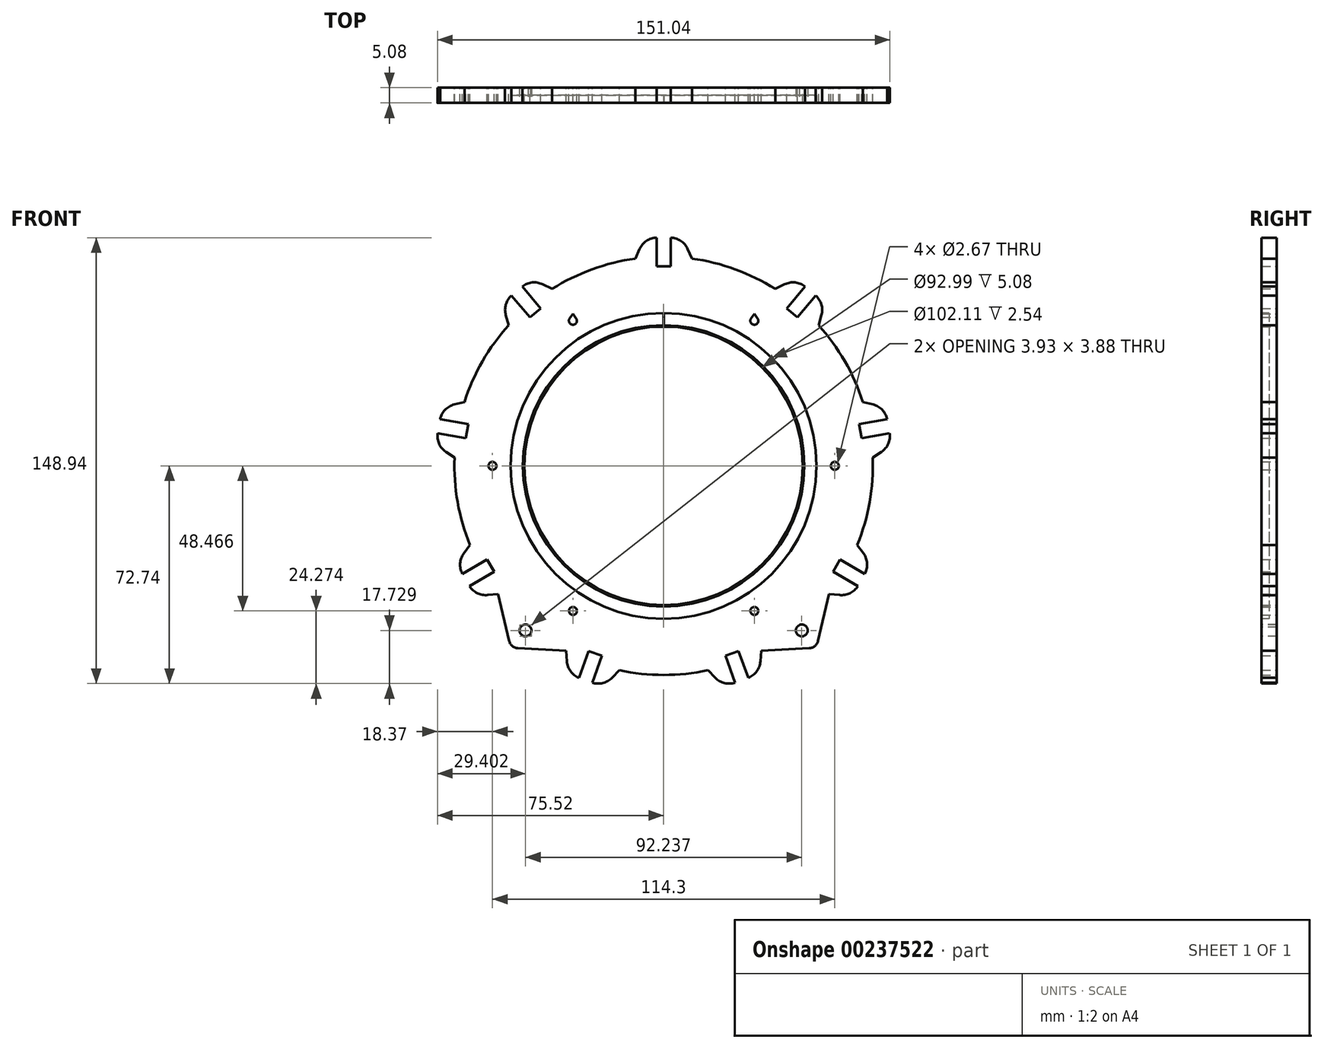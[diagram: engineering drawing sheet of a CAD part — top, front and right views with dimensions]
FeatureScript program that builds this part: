
annotation { "Feature Type Name" : "Feature", "Feature Type Description" : "" }
export const myFeature = defineFeature(function(context is Context, id is Id, definition is map)
    precondition{}
    {
        {
            var Q0;
            Q0=qCreatedBy(makeId("Front.planeOp"),FACE);
            var sketch = newSketch(context, id + "F0", { "sketchPlane" : qUnion([Q0])});
            skCircle(sketch, "E0", {"center": v(0, 0) * mm, "radius": 69.85 * mm});
            skCircle(sketch, "E1", {"center": v(0, 0) * mm, "radius": 46.5 * mm});
            skCircle(sketch, "E2", {"center": v(0, 0) * mm, "radius": 57.15 * mm, "construction": true});
            skPoint(sketch, "E3.center", {"position": v(0, -7.06) * mm});
            skLineSegment(sketch, "E4", {"start": v(-9.44, 69.2) * mm, "end": v(-8.02, 72.42) * mm});
            skLineSegment(sketch, "E5", {"start": v(-2.21, 76.2) * mm, "end": v(2.21, 76.2) * mm});
            skLineSegment(sketch, "E6", {"start": v(8.02, 72.42) * mm, "end": v(9.44, 69.2) * mm});
            skPoint(sketch, "E7", {"position": v(0, 76.2) * mm});
            skLineSegment(sketch, "E8", {"start": v(-2.35, 76.2) * mm, "end": v(-2.35, 66.67) * mm});
            skLineSegment(sketch, "E9", {"start": v(-2.35, 66.67) * mm, "end": v(2.35, 66.67) * mm});
            skLineSegment(sketch, "E10", {"start": v(2.35, 66.67) * mm, "end": v(2.35, 76.2) * mm});
            skPoint(sketch, "E11", {"position": v(0, 66.67) * mm});
            skPoint(sketch, "E12.visualSharp", {"position": v(-6.35, 76.2) * mm});
            skArc(sketch, "E12.filletArc", {"start": v(-2.21, 76.2) * mm, "mid": v(-5.68, 75.17) * mm, "end": v(-8.02, 72.42) * mm});
            skPoint(sketch, "E13.visualSharp", {"position": v(6.35, 76.2) * mm});
            skArc(sketch, "E13.filletArc", {"start": v(8.02, 72.42) * mm, "mid": v(5.68, 75.17) * mm, "end": v(2.21, 76.2) * mm});
            skCircle(sketch, "E14", {"center": v(0, 0) * mm, "radius": 66.72 * mm, "construction": true});
            skLineSegment(sketch, "E15.1.0", {"start": v(-51.72, 46.95) * mm, "end": v(-52.7, 50.32) * mm});
            skArc(sketch, "E15.1.1", {"start": v(-50.68, 56.95) * mm, "mid": v(-52.67, 53.93) * mm, "end": v(-52.7, 50.32) * mm});
            skLineSegment(sketch, "E15.1.2", {"start": v(-50.78, 56.86) * mm, "end": v(-44.66, 49.57) * mm});
            skLineSegment(sketch, "E15.1.3", {"start": v(-41.06, 52.59) * mm, "end": v(-47.18, 59.88) * mm});
            skArc(sketch, "E15.1.4", {"start": v(-40.4, 60.63) * mm, "mid": v(-43.97, 61.23) * mm, "end": v(-47.29, 59.8) * mm});
            skLineSegment(sketch, "E15.1.5", {"start": v(-40.4, 60.63) * mm, "end": v(-37.26, 59.08) * mm});
            skLineSegment(sketch, "E15.1.6", {"start": v(-44.66, 49.57) * mm, "end": v(-41.06, 52.59) * mm});
            skLineSegment(sketch, "E15.2.0", {"start": v(-69.8, 2.72) * mm, "end": v(-72.7, 4.68) * mm});
            skArc(sketch, "E15.2.1", {"start": v(-75.43, 11.05) * mm, "mid": v(-75.01, 7.46) * mm, "end": v(-72.7, 4.68) * mm});
            skLineSegment(sketch, "E15.2.2", {"start": v(-75.45, 10.92) * mm, "end": v(-66.07, 9.26) * mm});
            skLineSegment(sketch, "E15.2.3", {"start": v(-65.25, 13.9) * mm, "end": v(-74.63, 15.55) * mm});
            skArc(sketch, "E15.2.4", {"start": v(-69.92, 20.47) * mm, "mid": v(-73.04, 18.65) * mm, "end": v(-74.66, 15.41) * mm});
            skLineSegment(sketch, "E15.2.5", {"start": v(-69.92, 20.47) * mm, "end": v(-66.52, 21.31) * mm});
            skLineSegment(sketch, "E15.2.6", {"start": v(-66.07, 9.26) * mm, "end": v(-65.25, 13.9) * mm});
            skLineSegment(sketch, "E15.3.0", {"start": v(-55.22, -42.78) * mm, "end": v(-58.7, -43.15) * mm});
            skArc(sketch, "E15.3.1", {"start": v(-64.88, -40.02) * mm, "mid": v(-62.26, -42.5) * mm, "end": v(-58.7, -43.15) * mm});
            skLineSegment(sketch, "E15.3.2", {"start": v(-64.82, -40.13) * mm, "end": v(-56.57, -35.37) * mm});
            skLineSegment(sketch, "E15.3.3", {"start": v(-58.92, -31.3) * mm, "end": v(-67.17, -36.07) * mm});
            skArc(sketch, "E15.3.4", {"start": v(-66.72, -29.26) * mm, "mid": v(-67.94, -32.67) * mm, "end": v(-67.1, -36.18) * mm});
            skLineSegment(sketch, "E15.3.5", {"start": v(-66.72, -29.26) * mm, "end": v(-64.66, -26.43) * mm});
            skLineSegment(sketch, "E15.3.6", {"start": v(-56.57, -35.37) * mm, "end": v(-58.92, -31.3) * mm});
            skLineSegment(sketch, "E15.4.0", {"start": v(-14.8, -68.26) * mm, "end": v(-17.23, -70.8) * mm});
            skArc(sketch, "E15.4.1", {"start": v(-23.98, -72.36) * mm, "mid": v(-20.37, -72.58) * mm, "end": v(-17.23, -70.8) * mm});
            skLineSegment(sketch, "E15.4.2", {"start": v(-23.85, -72.4) * mm, "end": v(-20.6, -63.46) * mm});
            skLineSegment(sketch, "E15.4.3", {"start": v(-25.01, -61.85) * mm, "end": v(-28.27, -70.8) * mm});
            skArc(sketch, "E15.4.4", {"start": v(-32.3, -65.3) * mm, "mid": v(-31.05, -68.7) * mm, "end": v(-28.14, -70.85) * mm});
            skLineSegment(sketch, "E15.4.5", {"start": v(-32.3, -65.3) * mm, "end": v(-32.54, -61.8) * mm});
            skLineSegment(sketch, "E15.4.6", {"start": v(-20.6, -63.46) * mm, "end": v(-25.01, -61.85) * mm});
            skLineSegment(sketch, "E15.5.0", {"start": v(32.54, -61.8) * mm, "end": v(32.3, -65.3) * mm});
            skArc(sketch, "E15.5.1", {"start": v(28.14, -70.85) * mm, "mid": v(31.05, -68.7) * mm, "end": v(32.3, -65.3) * mm});
            skLineSegment(sketch, "E15.5.2", {"start": v(28.27, -70.8) * mm, "end": v(25.01, -61.85) * mm});
            skLineSegment(sketch, "E15.5.3", {"start": v(20.6, -63.46) * mm, "end": v(23.85, -72.4) * mm});
            skArc(sketch, "E15.5.4", {"start": v(17.23, -70.8) * mm, "mid": v(20.37, -72.58) * mm, "end": v(23.98, -72.36) * mm});
            skLineSegment(sketch, "E15.5.5", {"start": v(17.23, -70.8) * mm, "end": v(14.8, -68.26) * mm});
            skLineSegment(sketch, "E15.5.6", {"start": v(25.01, -61.85) * mm, "end": v(20.6, -63.46) * mm});
            skLineSegment(sketch, "E15.6.0", {"start": v(64.66, -26.43) * mm, "end": v(66.72, -29.26) * mm});
            skArc(sketch, "E15.6.1", {"start": v(67.1, -36.18) * mm, "mid": v(67.94, -32.67) * mm, "end": v(66.72, -29.26) * mm});
            skLineSegment(sketch, "E15.6.2", {"start": v(67.17, -36.07) * mm, "end": v(58.92, -31.3) * mm});
            skLineSegment(sketch, "E15.6.3", {"start": v(56.57, -35.37) * mm, "end": v(64.82, -40.13) * mm});
            skArc(sketch, "E15.6.4", {"start": v(58.7, -43.15) * mm, "mid": v(62.26, -42.5) * mm, "end": v(64.88, -40.02) * mm});
            skLineSegment(sketch, "E15.6.5", {"start": v(58.7, -43.15) * mm, "end": v(55.22, -42.78) * mm});
            skLineSegment(sketch, "E15.6.6", {"start": v(58.92, -31.3) * mm, "end": v(56.57, -35.37) * mm});
            skLineSegment(sketch, "E15.7.0", {"start": v(66.52, 21.31) * mm, "end": v(69.92, 20.47) * mm});
            skArc(sketch, "E15.7.1", {"start": v(74.66, 15.41) * mm, "mid": v(73.04, 18.65) * mm, "end": v(69.92, 20.47) * mm});
            skLineSegment(sketch, "E15.7.2", {"start": v(74.63, 15.55) * mm, "end": v(65.25, 13.9) * mm});
            skLineSegment(sketch, "E15.7.3", {"start": v(66.07, 9.26) * mm, "end": v(75.45, 10.92) * mm});
            skArc(sketch, "E15.7.4", {"start": v(72.7, 4.68) * mm, "mid": v(75.01, 7.46) * mm, "end": v(75.43, 11.05) * mm});
            skLineSegment(sketch, "E15.7.5", {"start": v(72.7, 4.68) * mm, "end": v(69.8, 2.72) * mm});
            skLineSegment(sketch, "E15.7.6", {"start": v(65.25, 13.9) * mm, "end": v(66.07, 9.26) * mm});
            skLineSegment(sketch, "E15.8.0", {"start": v(37.26, 59.08) * mm, "end": v(40.4, 60.63) * mm});
            skArc(sketch, "E15.8.1", {"start": v(47.29, 59.8) * mm, "mid": v(43.97, 61.23) * mm, "end": v(40.4, 60.63) * mm});
            skLineSegment(sketch, "E15.8.2", {"start": v(47.18, 59.88) * mm, "end": v(41.06, 52.59) * mm});
            skLineSegment(sketch, "E15.8.3", {"start": v(44.66, 49.57) * mm, "end": v(50.78, 56.86) * mm});
            skArc(sketch, "E15.8.4", {"start": v(52.7, 50.32) * mm, "mid": v(52.67, 53.93) * mm, "end": v(50.68, 56.95) * mm});
            skLineSegment(sketch, "E15.8.5", {"start": v(52.7, 50.32) * mm, "end": v(51.72, 46.95) * mm});
            skLineSegment(sketch, "E15.8.6", {"start": v(41.06, 52.59) * mm, "end": v(44.66, 49.57) * mm});
            skCircle(sketch, "E16", {"center": v(57.15, 0) * mm, "radius": 1.33 * mm});
            skCircle(sketch, "E17", {"center": v(30.28, 48.47) * mm, "radius": 1.33 * mm});
            skCircle(sketch, "E18", {"center": v(30.28, -48.47) * mm, "radius": 1.33 * mm});
            skLineSegment(sketch, "E19", {"start": v(0, 0) * mm, "end": v(30.28, -48.47) * mm, "construction": true});
            skLineSegment(sketch, "E20", {"start": v(30.28, 48.47) * mm, "end": v(0, 0) * mm, "construction": true});
            skCircle(sketch, "E21.MirrorC", {"center": v(-30.28, -48.47) * mm, "radius": 1.33 * mm});
            skCircle(sketch, "E22.MirrorC", {"center": v(-57.15, 0) * mm, "radius": 1.33 * mm});
            skCircle(sketch, "E23.MirrorC", {"center": v(-30.28, 48.47) * mm, "radius": 1.33 * mm});
            skLineSegment(sketch, "E24", {"start": v(31.38, 49.23) * mm, "end": v(30.28, 50.78) * mm});
            skLineSegment(sketch, "E25", {"start": v(30.28, 50.78) * mm, "end": v(29.2, 49.23) * mm});
            skLineSegment(sketch, "E26", {"start": v(-31.38, 49.23) * mm, "end": v(-30.28, 50.78) * mm});
            skLineSegment(sketch, "E27", {"start": v(-30.28, 50.78) * mm, "end": v(-29.2, 49.23) * mm});
            skArc(sketch, "E28", {"start": v(-2.21, 76.2) * mm, "mid": v(-8.62, 74.13) * mm, "end": v(-12.61, 68.7) * mm});
            skArc(sketch, "E29", {"start": v(12.61, 68.7) * mm, "mid": v(8.7, 74.13) * mm, "end": v(2.35, 76.2) * mm});
            skSolve(sketch);
        }
        {
            var Q0;
            Q0=makeQuery(id+"F0.imprint","IMPRINT",FACE,{"disambiguationData":[TD([[makeQuery(id+"F0.imprint","IMPRINT",EDGE,{"derivedFrom":sQuery(id+"F0.wireOp",EDGE,"E1")}),-1.0]])]});
            var Q1;
            {var subQ0=sQuery(id+"F0.wireOp",EDGE,"E15.1.5");Q1=makeQuery(id+"F0.imprint","IMPRINT",FACE,{"disambiguationData":[TD([[makeQuery(id+"F0.imprint","IMPRINT",EDGE,{"derivedFrom":subQ0}),-1.0]])]});}
            var Q2;
            {var subQ0=sQuery(id+"F0.wireOp",EDGE,"E15.1.0");Q2=makeQuery(id+"F0.imprint","IMPRINT",FACE,{"disambiguationData":[TD([[makeQuery(id+"F0.imprint","IMPRINT",EDGE,{"derivedFrom":subQ0}),-1.0]])]});}
            var Q3;
            {var subQ0=sQuery(id+"F0.wireOp",EDGE,"E4");Q3=makeQuery(id+"F0.imprint","IMPRINT",FACE,{"disambiguationData":[TD([[makeQuery(id+"F0.imprint","IMPRINT",EDGE,{"derivedFrom":subQ0}),-1.0]])]});}
            var Q4;
            {var subQ0=sQuery(id+"F0.wireOp",EDGE,"E6");Q4=makeQuery(id+"F0.imprint","IMPRINT",FACE,{"disambiguationData":[TD([[makeQuery(id+"F0.imprint","IMPRINT",EDGE,{"derivedFrom":subQ0}),-1.0]])]});}
            var Q5;
            {var subQ0=sQuery(id+"F0.wireOp",EDGE,"E15.8.0");Q5=makeQuery(id+"F0.imprint","IMPRINT",FACE,{"disambiguationData":[TD([[makeQuery(id+"F0.imprint","IMPRINT",EDGE,{"derivedFrom":subQ0}),-1.0]])]});}
            var Q6;
            {var subQ0=sQuery(id+"F0.wireOp",EDGE,"E15.8.5");Q6=makeQuery(id+"F0.imprint","IMPRINT",FACE,{"disambiguationData":[TD([[makeQuery(id+"F0.imprint","IMPRINT",EDGE,{"derivedFrom":subQ0}),-1.0]])]});}
            var Q7;
            {var subQ0=sQuery(id+"F0.wireOp",EDGE,"E15.7.0");Q7=makeQuery(id+"F0.imprint","IMPRINT",FACE,{"disambiguationData":[TD([[makeQuery(id+"F0.imprint","IMPRINT",EDGE,{"derivedFrom":subQ0}),-1.0]])]});}
            var Q8;
            {var subQ0=sQuery(id+"F0.wireOp",EDGE,"E15.7.5");Q8=makeQuery(id+"F0.imprint","IMPRINT",FACE,{"disambiguationData":[TD([[makeQuery(id+"F0.imprint","IMPRINT",EDGE,{"derivedFrom":subQ0}),-1.0]])]});}
            var Q9;
            {var subQ0=sQuery(id+"F0.wireOp",EDGE,"E15.6.0");Q9=makeQuery(id+"F0.imprint","IMPRINT",FACE,{"disambiguationData":[TD([[makeQuery(id+"F0.imprint","IMPRINT",EDGE,{"derivedFrom":subQ0}),-1.0]])]});}
            var Q10;
            {var subQ0=sQuery(id+"F0.wireOp",EDGE,"E15.6.5");Q10=makeQuery(id+"F0.imprint","IMPRINT",FACE,{"disambiguationData":[TD([[makeQuery(id+"F0.imprint","IMPRINT",EDGE,{"derivedFrom":subQ0}),-1.0]])]});}
            var Q11;
            {var subQ0=sQuery(id+"F0.wireOp",EDGE,"E15.5.5");Q11=makeQuery(id+"F0.imprint","IMPRINT",FACE,{"disambiguationData":[TD([[makeQuery(id+"F0.imprint","IMPRINT",EDGE,{"derivedFrom":subQ0}),-1.0]])]});}
            var Q12;
            {var subQ0=sQuery(id+"F0.wireOp",EDGE,"E15.5.0");Q12=makeQuery(id+"F0.imprint","IMPRINT",FACE,{"disambiguationData":[TD([[makeQuery(id+"F0.imprint","IMPRINT",EDGE,{"derivedFrom":subQ0}),-1.0]])]});}
            var Q13;
            {var subQ0=sQuery(id+"F0.wireOp",EDGE,"E15.4.5");Q13=makeQuery(id+"F0.imprint","IMPRINT",FACE,{"disambiguationData":[TD([[makeQuery(id+"F0.imprint","IMPRINT",EDGE,{"derivedFrom":subQ0}),-1.0]])]});}
            var Q14;
            {var subQ0=sQuery(id+"F0.wireOp",EDGE,"E15.4.0");Q14=makeQuery(id+"F0.imprint","IMPRINT",FACE,{"disambiguationData":[TD([[makeQuery(id+"F0.imprint","IMPRINT",EDGE,{"derivedFrom":subQ0}),-1.0]])]});}
            var Q15;
            {var subQ0=sQuery(id+"F0.wireOp",EDGE,"E15.3.0");Q15=makeQuery(id+"F0.imprint","IMPRINT",FACE,{"disambiguationData":[TD([[makeQuery(id+"F0.imprint","IMPRINT",EDGE,{"derivedFrom":subQ0}),-1.0]])]});}
            var Q16;
            {var subQ0=sQuery(id+"F0.wireOp",EDGE,"E15.3.5");Q16=makeQuery(id+"F0.imprint","IMPRINT",FACE,{"disambiguationData":[TD([[makeQuery(id+"F0.imprint","IMPRINT",EDGE,{"derivedFrom":subQ0}),-1.0]])]});}
            var Q17;
            {var subQ0=sQuery(id+"F0.wireOp",EDGE,"E15.2.0");Q17=makeQuery(id+"F0.imprint","IMPRINT",FACE,{"disambiguationData":[TD([[makeQuery(id+"F0.imprint","IMPRINT",EDGE,{"derivedFrom":subQ0}),-1.0]])]});}
            var Q18;
            {var subQ0=sQuery(id+"F0.wireOp",EDGE,"E15.2.5");Q18=makeQuery(id+"F0.imprint","IMPRINT",FACE,{"disambiguationData":[TD([[makeQuery(id+"F0.imprint","IMPRINT",EDGE,{"derivedFrom":subQ0}),-1.0]])]});}
            extrude(context, id + "F1", {"entities" : qUnion([Q0, Q1, Q2, Q3, Q4, Q5, Q6, Q7, Q8, Q9, Q10, Q11, Q12, Q13, Q14, Q15, Q16, Q17, Q18]), "depth" : 5.08 * mm});
        }
        {
            var Q0;
            Q0=makeQuery(id+"F1.opExtrude","CAP_FACE",FACE,{"disambiguationData":[OSD([sQuery(id+"F0.wireOp",EDGE,"E0"),sQuery(id+"F0.wireOp",EDGE,"E1"),sQuery(id+"F0.wireOp",EDGE,"s7rXqqL2-3z2l-88EV-UIsY-hwb08Po9ZJjJ"),sQuery(id+"F0.wireOp",EDGE,"E3.1.0"),sQuery(id+"F0.wireOp",EDGE,"E3.2.0"),sQuery(id+"F0.wireOp",EDGE,"E3.3.0"),sQuery(id+"F0.wireOp",EDGE,"E4"),sQuery(id+"F0.wireOp",EDGE,"E6"),sQuery(id+"F0.wireOp",EDGE,"E8"),sQuery(id+"F0.wireOp",EDGE,"E9"),sQuery(id+"F0.wireOp",EDGE,"E10"),sQuery(id+"F0.wireOp",EDGE,"E12.filletArc"),sQuery(id+"F0.wireOp",EDGE,"E13.filletArc"),sQuery(id+"F0.wireOp",EDGE,"e3144966-756d-47fd-8283-5f46bd2110e0.1.0"),sQuery(id+"F0.wireOp",EDGE,"e3144966-756d-47fd-8283-5f46bd2110e0.1.1"),sQuery(id+"F0.wireOp",EDGE,"e3144966-756d-47fd-8283-5f46bd2110e0.1.2"),sQuery(id+"F0.wireOp",EDGE,"e3144966-756d-47fd-8283-5f46bd2110e0.1.3"),sQuery(id+"F0.wireOp",EDGE,"e3144966-756d-47fd-8283-5f46bd2110e0.1.4"),sQuery(id+"F0.wireOp",EDGE,"e3144966-756d-47fd-8283-5f46bd2110e0.1.6"),sQuery(id+"F0.wireOp",EDGE,"e3144966-756d-47fd-8283-5f46bd2110e0.1.7"),sQuery(id+"F0.wireOp",EDGE,"e3144966-756d-47fd-8283-5f46bd2110e0.2.0"),sQuery(id+"F0.wireOp",EDGE,"e3144966-756d-47fd-8283-5f46bd2110e0.2.1"),sQuery(id+"F0.wireOp",EDGE,"e3144966-756d-47fd-8283-5f46bd2110e0.2.2"),sQuery(id+"F0.wireOp",EDGE,"e3144966-756d-47fd-8283-5f46bd2110e0.2.3"),sQuery(id+"F0.wireOp",EDGE,"e3144966-756d-47fd-8283-5f46bd2110e0.2.4"),sQuery(id+"F0.wireOp",EDGE,"e3144966-756d-47fd-8283-5f46bd2110e0.2.6"),sQuery(id+"F0.wireOp",EDGE,"e3144966-756d-47fd-8283-5f46bd2110e0.2.7"),sQuery(id+"F0.wireOp",EDGE,"e3144966-756d-47fd-8283-5f46bd2110e0.3.0"),sQuery(id+"F0.wireOp",EDGE,"e3144966-756d-47fd-8283-5f46bd2110e0.3.1"),sQuery(id+"F0.wireOp",EDGE,"e3144966-756d-47fd-8283-5f46bd2110e0.3.2"),sQuery(id+"F0.wireOp",EDGE,"e3144966-756d-47fd-8283-5f46bd2110e0.3.3"),sQuery(id+"F0.wireOp",EDGE,"e3144966-756d-47fd-8283-5f46bd2110e0.3.4"),sQuery(id+"F0.wireOp",EDGE,"e3144966-756d-47fd-8283-5f46bd2110e0.3.6"),sQuery(id+"F0.wireOp",EDGE,"e3144966-756d-47fd-8283-5f46bd2110e0.3.7"),sQuery(id+"F0.wireOp",EDGE,"e3144966-756d-47fd-8283-5f46bd2110e0.4.0"),sQuery(id+"F0.wireOp",EDGE,"e3144966-756d-47fd-8283-5f46bd2110e0.4.1"),sQuery(id+"F0.wireOp",EDGE,"e3144966-756d-47fd-8283-5f46bd2110e0.4.2"),sQuery(id+"F0.wireOp",EDGE,"e3144966-756d-47fd-8283-5f46bd2110e0.4.3"),sQuery(id+"F0.wireOp",EDGE,"e3144966-756d-47fd-8283-5f46bd2110e0.4.4"),sQuery(id+"F0.wireOp",EDGE,"e3144966-756d-47fd-8283-5f46bd2110e0.4.6"),sQuery(id+"F0.wireOp",EDGE,"e3144966-756d-47fd-8283-5f46bd2110e0.4.7"),sQuery(id+"F0.wireOp",EDGE,"e3144966-756d-47fd-8283-5f46bd2110e0.5.0"),sQuery(id+"F0.wireOp",EDGE,"e3144966-756d-47fd-8283-5f46bd2110e0.5.1"),sQuery(id+"F0.wireOp",EDGE,"e3144966-756d-47fd-8283-5f46bd2110e0.5.2"),sQuery(id+"F0.wireOp",EDGE,"e3144966-756d-47fd-8283-5f46bd2110e0.5.3"),sQuery(id+"F0.wireOp",EDGE,"e3144966-756d-47fd-8283-5f46bd2110e0.5.4"),sQuery(id+"F0.wireOp",EDGE,"e3144966-756d-47fd-8283-5f46bd2110e0.5.6"),sQuery(id+"F0.wireOp",EDGE,"e3144966-756d-47fd-8283-5f46bd2110e0.5.7"),sQuery(id+"F0.wireOp",EDGE,"e3144966-756d-47fd-8283-5f46bd2110e0.6.0"),sQuery(id+"F0.wireOp",EDGE,"e3144966-756d-47fd-8283-5f46bd2110e0.6.1"),sQuery(id+"F0.wireOp",EDGE,"e3144966-756d-47fd-8283-5f46bd2110e0.6.2"),sQuery(id+"F0.wireOp",EDGE,"e3144966-756d-47fd-8283-5f46bd2110e0.6.3"),sQuery(id+"F0.wireOp",EDGE,"e3144966-756d-47fd-8283-5f46bd2110e0.6.4"),sQuery(id+"F0.wireOp",EDGE,"e3144966-756d-47fd-8283-5f46bd2110e0.6.6"),sQuery(id+"F0.wireOp",EDGE,"e3144966-756d-47fd-8283-5f46bd2110e0.6.7"),sQuery(id+"F0.wireOp",EDGE,"e3144966-756d-47fd-8283-5f46bd2110e0.7.0"),sQuery(id+"F0.wireOp",EDGE,"e3144966-756d-47fd-8283-5f46bd2110e0.7.1"),sQuery(id+"F0.wireOp",EDGE,"e3144966-756d-47fd-8283-5f46bd2110e0.7.2"),sQuery(id+"F0.wireOp",EDGE,"e3144966-756d-47fd-8283-5f46bd2110e0.7.3"),sQuery(id+"F0.wireOp",EDGE,"e3144966-756d-47fd-8283-5f46bd2110e0.7.4"),sQuery(id+"F0.wireOp",EDGE,"e3144966-756d-47fd-8283-5f46bd2110e0.7.6"),sQuery(id+"F0.wireOp",EDGE,"e3144966-756d-47fd-8283-5f46bd2110e0.7.7"),sQuery(id+"F0.wireOp",EDGE,"e3144966-756d-47fd-8283-5f46bd2110e0.8.0"),sQuery(id+"F0.wireOp",EDGE,"e3144966-756d-47fd-8283-5f46bd2110e0.8.1"),sQuery(id+"F0.wireOp",EDGE,"e3144966-756d-47fd-8283-5f46bd2110e0.8.2"),sQuery(id+"F0.wireOp",EDGE,"e3144966-756d-47fd-8283-5f46bd2110e0.8.3"),sQuery(id+"F0.wireOp",EDGE,"e3144966-756d-47fd-8283-5f46bd2110e0.8.4"),sQuery(id+"F0.wireOp",EDGE,"e3144966-756d-47fd-8283-5f46bd2110e0.8.6"),sQuery(id+"F0.wireOp",EDGE,"e3144966-756d-47fd-8283-5f46bd2110e0.8.7")])],"isStart":false});
            var sketch = newSketch(context, id + "F2", { "sketchPlane" : qUnion([Q0])});
            skCircle(sketch, "E30", {"center": v(0, 0) * mm, "radius": 47 * mm});
            skCircle(sketch, "E31", {"center": v(0, 0) * mm, "radius": 51.05 * mm});
            skSolve(sketch);
        }
        {
            var Q0;
            Q0=makeQuery(id+"F2.imprint","IMPRINT",FACE,{"disambiguationData":[TD([[makeQuery(id+"F2.imprint","IMPRINT",EDGE,{"derivedFrom":sQuery(id+"F2.wireOp",EDGE,"E31")}),1.0]])]});
            extrude(context, id + "F3", {"entities" : qUnion([Q0]), "operationType" : NewBodyOperationType.REMOVE, "oppositeDirection" : true, "depth" : 2.54 * mm});
        }
        {
            var Q0;
            {var subQ0=sQuery(id+"F0.wireOp",EDGE,"E15.5.2");var subQ1=sQuery(id+"F0.wireOp",EDGE,"E15.5.0");var subQ2=sQuery(id+"F0.wireOp",EDGE,"E15.5.5");var subQ3=sQuery(id+"F0.wireOp",EDGE,"E15.4.5");var subQ4=sQuery(id+"F0.wireOp",EDGE,"E15.4.6");var subQ5=sQuery(id+"F0.wireOp",EDGE,"E15.4.4");var subQ6=sQuery(id+"F0.wireOp",EDGE,"E15.5.3");var subQ7=sQuery(id+"F0.wireOp",EDGE,"E15.4.2");var subQ8=sQuery(id+"F0.wireOp",EDGE,"E15.4.0");var subQ9=sQuery(id+"F0.wireOp",EDGE,"E15.3.5");var subQ10=sQuery(id+"F0.wireOp",EDGE,"E15.3.3");var subQ11=sQuery(id+"F0.wireOp",EDGE,"E15.2.5");var subQ12=sQuery(id+"F0.wireOp",EDGE,"E15.3.1");var subQ13=sQuery(id+"F0.wireOp",EDGE,"E29");var subQ14=sQuery(id+"F0.wireOp",EDGE,"E15.5.4");var subQ15=sQuery(id+"F0.wireOp",EDGE,"E15.4.3");var subQ16=sQuery(id+"F0.wireOp",EDGE,"E15.4.1");var subQ17=sQuery(id+"F0.wireOp",EDGE,"E15.3.0");var subQ18=sQuery(id+"F0.wireOp",EDGE,"E28");var subQ19=sQuery(id+"F0.wireOp",EDGE,"E15.2.6");var subQ20=sQuery(id+"F0.wireOp",EDGE,"E27");var subQ21=sQuery(id+"F0.wireOp",EDGE,"E15.2.4");var subQ22=sQuery(id+"F0.wireOp",EDGE,"E25");var subQ23=sQuery(id+"F0.wireOp",EDGE,"E15.3.6");var subQ24=sQuery(id+"F0.wireOp",EDGE,"E15.3.4");var subQ25=sQuery(id+"F0.wireOp",EDGE,"E15.2.3");var subQ26=sQuery(id+"F0.wireOp",EDGE,"E0");var subQ27=sQuery(id+"F0.wireOp",EDGE,"E15.6.5");var subQ28=sQuery(id+"F0.wireOp",EDGE,"E15.7.4");var subQ29=sQuery(id+"F0.wireOp",EDGE,"E15.1.1");var subQ30=sQuery(id+"F0.wireOp",EDGE,"E17");var subQ31=sQuery(id+"F0.wireOp",EDGE,"E15.2.0");var subQ32=sQuery(id+"F0.wireOp",EDGE,"E15.2.2");var subQ33=sQuery(id+"F0.wireOp",EDGE,"E23.MirrorC");var subQ34=sQuery(id+"F0.wireOp",EDGE,"E15.7.0");var subQ35=sQuery(id+"F0.wireOp",EDGE,"E15.8.5");var subQ36=sQuery(id+"F0.wireOp",EDGE,"E15.8.0");var subQ37=sQuery(id+"F0.wireOp",EDGE,"E15.8.4");var subQ38=sQuery(id+"F0.wireOp",EDGE,"E15.1.5");var subQ39=sQuery(id+"F0.wireOp",EDGE,"E15.5.1");var subQ40=sQuery(id+"F0.wireOp",EDGE,"E15.1.0");var subQ41=sQuery(id+"F0.wireOp",EDGE,"E9");var subQ42=sQuery(id+"F0.wireOp",EDGE,"E15.8.1");var subQ43=sQuery(id+"F0.wireOp",EDGE,"E15.1.2");var subQ44=sQuery(id+"F0.wireOp",EDGE,"E15.7.3");var subQ45=sQuery(id+"F0.wireOp",EDGE,"E15.1.4");var subQ46=sQuery(id+"F0.wireOp",EDGE,"E8");var subQ47=sQuery(id+"F0.wireOp",EDGE,"E15.3.2");var subQ48=sQuery(id+"F0.wireOp",EDGE,"E15.2.1");var subQ49=sQuery(id+"F0.wireOp",EDGE,"E15.1.6");var subQ50=sQuery(id+"F0.wireOp",EDGE,"E15.8.3");var subQ51=sQuery(id+"F0.wireOp",EDGE,"E10");var subQ52=sQuery(id+"F0.wireOp",EDGE,"E15.8.2");var subQ53=sQuery(id+"F0.wireOp",EDGE,"E15.6.0");var subQ54=sQuery(id+"F0.wireOp",EDGE,"E15.7.5");var subQ55=sQuery(id+"F0.wireOp",EDGE,"E15.1.3");var subQ56=sQuery(id+"F0.wireOp",EDGE,"E15.5.6");var subQ57=sQuery(id+"F0.wireOp",EDGE,"E26");var subQ58=sQuery(id+"F0.wireOp",EDGE,"E15.6.1");var subQ59=sQuery(id+"F0.wireOp",EDGE,"E15.6.2");var subQ60=sQuery(id+"F0.wireOp",EDGE,"E15.6.3");var subQ61=sQuery(id+"F0.wireOp",EDGE,"E15.6.4");var subQ62=sQuery(id+"F0.wireOp",EDGE,"E24");var subQ63=sQuery(id+"F0.wireOp",EDGE,"E15.6.6");var subQ64=sQuery(id+"F0.wireOp",EDGE,"E15.7.1");var subQ65=sQuery(id+"F0.wireOp",EDGE,"E15.7.2");var subQ66=sQuery(id+"F0.wireOp",EDGE,"E15.7.6");var subQ67=sQuery(id+"F0.wireOp",EDGE,"E15.8.6");var subQ68=sQuery(id+"F0.wireOp",EDGE,"E16");var subQ69=sQuery(id+"F0.wireOp",EDGE,"E18");var subQ70=sQuery(id+"F0.wireOp",EDGE,"E21.MirrorC");var subQ71=sQuery(id+"F0.wireOp",EDGE,"E22.MirrorC");Q0=makeQuery(id+"F3.boolean.opBoolean","SPLIT",FACE,{"disambiguationData":[TD([makeQuery(id+"F1.opExtrude","SWEPT_FACE",FACE,{"disambiguationData":[OSD([subQ46])]})])],"derivedFrom":makeQuery(id+"F1.opExtrude","CAP_FACE",FACE,{"disambiguationData":[OSD([subQ26,sQuery(id+"F0.wireOp",EDGE,"E1"),subQ46,subQ41,subQ51,subQ40,subQ29,subQ43,subQ55,subQ45,subQ38,subQ49,subQ31,subQ48,subQ32,subQ25,subQ21,subQ11,subQ19,subQ17,subQ12,subQ47,subQ10,subQ24,subQ9,subQ23,subQ8,subQ16,subQ7,subQ15,subQ5,subQ3,subQ4,subQ1,subQ39,subQ0,subQ6,subQ14,subQ2,subQ56,subQ53,subQ58,subQ59,subQ60,subQ61,subQ27,subQ63,subQ34,subQ64,subQ65,subQ44,subQ28,subQ54,subQ66,subQ36,subQ42,subQ52,subQ50,subQ37,subQ35,subQ67,subQ68,subQ30,subQ69,subQ70,subQ71,subQ33,subQ62,subQ22,subQ57,subQ20,subQ18,subQ13])],"isStart":false})});}
            var sketch = newSketch(context, id + "F4", { "sketchPlane" : qUnion([Q0])});
            skLineSegment(sketch, "E32", {"start": v(-0.03, 51.05) * mm, "end": v(-0.03, 46.99) * mm});
            skLineSegment(sketch, "E33", {"start": v(0.03, 46.99) * mm, "end": v(0.03, 51.05) * mm});
            skArc(sketch, "E34", {"start": v(0.03, 46.99) * mm, "mid": v(0, 46.99) * mm, "end": v(-0.03, 46.99) * mm});
            skArc(sketch, "E35", {"start": v(0.03, 51.05) * mm, "mid": v(0, 51.05) * mm, "end": v(-0.03, 51.05) * mm});
            skPoint(sketch, "E36.positionSnap0", {"position": v(0, 47) * mm});
            skSolve(sketch);
        }
        {
            var Q0;
            Q0 = qSketchRegion(id + "F4", true);
            var Q1;
            Q1=makeQuery(id+"F3.boolean.opBoolean","COPY",FACE,{"derivedFrom":makeQuery(id+"F3.opExtrude","CAP_FACE",FACE,{"disambiguationData":[OSD([sQuery(id+"F2.wireOp",EDGE,"E30"),sQuery(id+"F2.wireOp",EDGE,"E31")])],"isStart":false})});
            extrude(context, id + "F5", {"entities" : qUnion([Q0]), "operationType" : NewBodyOperationType.ADD, "endBound" : BoundingType.UP_TO_SURFACE, "oppositeDirection" : true, "endBoundEntityFace" : qUnion([Q1]), "depth" : 25.4 * mm});
        }
        {
            var Q0;
            {var subQ0=sQuery(id+"F4.wireOp",EDGE,"E35");var subQ1=sQuery(id+"F4.wireOp",EDGE,"E34");var subQ2=sQuery(id+"F4.wireOp",EDGE,"E33");var subQ3=sQuery(id+"F4.wireOp",EDGE,"E32");var subQ4=sQuery(id+"F0.wireOp",EDGE,"E1");var subQ5=sQuery(id+"F0.wireOp",EDGE,"E27");var subQ6=sQuery(id+"F0.wireOp",EDGE,"E26");var subQ7=sQuery(id+"F0.wireOp",EDGE,"E25");var subQ8=sQuery(id+"F0.wireOp",EDGE,"E24");var subQ9=sQuery(id+"F0.wireOp",EDGE,"E23.MirrorC");var subQ10=sQuery(id+"F0.wireOp",EDGE,"E22.MirrorC");var subQ11=sQuery(id+"F0.wireOp",EDGE,"E21.MirrorC");var subQ12=sQuery(id+"F0.wireOp",EDGE,"E18");var subQ13=sQuery(id+"F0.wireOp",EDGE,"E17");var subQ14=sQuery(id+"F0.wireOp",EDGE,"E16");var subQ15=sQuery(id+"F0.wireOp",EDGE,"E15.8.6");var subQ16=sQuery(id+"F0.wireOp",EDGE,"E15.8.5");var subQ17=sQuery(id+"F0.wireOp",EDGE,"E15.8.4");var subQ18=sQuery(id+"F0.wireOp",EDGE,"E15.8.3");var subQ19=sQuery(id+"F0.wireOp",EDGE,"E15.8.2");var subQ20=sQuery(id+"F0.wireOp",EDGE,"E15.8.1");var subQ21=sQuery(id+"F0.wireOp",EDGE,"E15.8.0");var subQ22=sQuery(id+"F0.wireOp",EDGE,"E15.7.6");var subQ23=sQuery(id+"F0.wireOp",EDGE,"E15.7.5");var subQ24=sQuery(id+"F0.wireOp",EDGE,"E15.7.4");var subQ25=sQuery(id+"F0.wireOp",EDGE,"E15.7.3");var subQ26=sQuery(id+"F0.wireOp",EDGE,"E15.7.2");var subQ27=sQuery(id+"F0.wireOp",EDGE,"E15.7.1");var subQ28=sQuery(id+"F0.wireOp",EDGE,"E15.7.0");var subQ29=sQuery(id+"F0.wireOp",EDGE,"E15.6.6");var subQ30=sQuery(id+"F0.wireOp",EDGE,"E15.6.5");var subQ31=sQuery(id+"F0.wireOp",EDGE,"E15.6.4");var subQ32=sQuery(id+"F0.wireOp",EDGE,"E15.6.3");var subQ33=sQuery(id+"F0.wireOp",EDGE,"E15.6.2");var subQ34=sQuery(id+"F0.wireOp",EDGE,"E15.6.1");var subQ35=sQuery(id+"F0.wireOp",EDGE,"E15.6.0");var subQ36=sQuery(id+"F0.wireOp",EDGE,"E15.5.6");var subQ37=sQuery(id+"F0.wireOp",EDGE,"E15.5.5");var subQ38=sQuery(id+"F0.wireOp",EDGE,"E15.5.4");var subQ39=sQuery(id+"F0.wireOp",EDGE,"E15.5.3");var subQ40=sQuery(id+"F0.wireOp",EDGE,"E15.5.2");var subQ41=sQuery(id+"F0.wireOp",EDGE,"E15.5.1");var subQ42=sQuery(id+"F0.wireOp",EDGE,"E15.5.0");var subQ43=sQuery(id+"F0.wireOp",EDGE,"E15.4.6");var subQ44=sQuery(id+"F0.wireOp",EDGE,"E15.4.5");var subQ45=sQuery(id+"F0.wireOp",EDGE,"E15.4.4");var subQ46=sQuery(id+"F0.wireOp",EDGE,"E15.4.3");var subQ47=sQuery(id+"F0.wireOp",EDGE,"E15.4.2");var subQ48=sQuery(id+"F0.wireOp",EDGE,"E15.4.1");var subQ49=sQuery(id+"F0.wireOp",EDGE,"E15.4.0");var subQ50=sQuery(id+"F0.wireOp",EDGE,"E15.3.6");var subQ51=sQuery(id+"F0.wireOp",EDGE,"E15.3.5");var subQ52=sQuery(id+"F0.wireOp",EDGE,"E15.3.4");var subQ53=sQuery(id+"F0.wireOp",EDGE,"E15.3.3");var subQ54=sQuery(id+"F0.wireOp",EDGE,"E15.3.2");var subQ55=sQuery(id+"F0.wireOp",EDGE,"E15.3.1");var subQ56=sQuery(id+"F0.wireOp",EDGE,"E15.3.0");var subQ57=sQuery(id+"F0.wireOp",EDGE,"E15.2.6");var subQ58=sQuery(id+"F0.wireOp",EDGE,"E15.2.5");var subQ59=sQuery(id+"F0.wireOp",EDGE,"E15.2.4");var subQ60=sQuery(id+"F0.wireOp",EDGE,"E15.2.3");var subQ61=sQuery(id+"F0.wireOp",EDGE,"E15.2.2");var subQ62=sQuery(id+"F0.wireOp",EDGE,"E15.2.1");var subQ63=sQuery(id+"F0.wireOp",EDGE,"E15.2.0");var subQ64=sQuery(id+"F0.wireOp",EDGE,"E15.1.6");var subQ65=sQuery(id+"F0.wireOp",EDGE,"E15.1.5");var subQ66=sQuery(id+"F0.wireOp",EDGE,"E15.1.4");var subQ67=sQuery(id+"F0.wireOp",EDGE,"E15.1.3");var subQ68=sQuery(id+"F0.wireOp",EDGE,"E15.1.2");var subQ69=sQuery(id+"F0.wireOp",EDGE,"E15.1.1");var subQ70=sQuery(id+"F0.wireOp",EDGE,"E15.1.0");var subQ71=sQuery(id+"F0.wireOp",EDGE,"E13.filletArc");var subQ72=sQuery(id+"F0.wireOp",EDGE,"E12.filletArc");var subQ73=sQuery(id+"F0.wireOp",EDGE,"E10");var subQ74=sQuery(id+"F0.wireOp",EDGE,"E9");var subQ75=sQuery(id+"F0.wireOp",EDGE,"E8");var subQ76=sQuery(id+"F0.wireOp",EDGE,"E6");var subQ77=sQuery(id+"F0.wireOp",EDGE,"E4");var subQ78=sQuery(id+"F0.wireOp",EDGE,"E0");var subQ79=makeQuery(id+"F1.opExtrude","CAP_FACE",FACE,{"disambiguationData":[OSD([subQ78,subQ4,subQ77,subQ76,subQ75,subQ74,subQ73,subQ72,subQ71,subQ70,subQ69,subQ68,subQ67,subQ66,subQ65,subQ64,subQ63,subQ62,subQ61,subQ60,subQ59,subQ58,subQ57,subQ56,subQ55,subQ54,subQ53,subQ52,subQ51,subQ50,subQ49,subQ48,subQ47,subQ46,subQ45,subQ44,subQ43,subQ42,subQ41,subQ40,subQ39,subQ38,subQ37,subQ36,subQ35,subQ34,subQ33,subQ32,subQ31,subQ30,subQ29,subQ28,subQ27,subQ26,subQ25,subQ24,subQ23,subQ22,subQ21,subQ20,subQ19,subQ18,subQ17,subQ16,subQ15,subQ14,subQ13,subQ12,subQ11,subQ10,subQ9,subQ8,subQ7,subQ6,subQ5])],"isStart":false});Q0=makeQuery(id+"F3rWmamWYXU4C0m_1.1.F5.boolean.opBoolean","MERGE",FACE,{"derivedFrom":[makeQuery(id+"F5.boolean.opBoolean","MERGE",FACE,{"derivedFrom":[makeQuery(id+"F3.boolean.opBoolean","SPLIT",FACE,{"disambiguationData":[TD([makeQuery(id+"F1.opExtrude","SWEPT_FACE",FACE,{"disambiguationData":[OSD([subQ77])]})])],"derivedFrom":subQ79}),makeQuery(id+"F3.boolean.opBoolean","SPLIT",FACE,{"disambiguationData":[TD([makeQuery(id+"F1.opExtrude","SWEPT_FACE",FACE,{"disambiguationData":[OSD([subQ4])]})])],"derivedFrom":subQ79}),makeQuery(id+"F5.opExtrude","CAP_FACE",FACE,{"disambiguationData":[OSD([subQ3,subQ2,subQ1,subQ0])],"isStart":true})]}),makeQuery(id+"F3rWmamWYXU4C0m_1.1.F5.opExtrude","CAP_FACE",FACE,{"disambiguationData":[OSD([subQ3,subQ2,subQ1,subQ0])],"isStart":true})]});}
            var sketch = newSketch(context, id + "F6", { "sketchPlane" : qUnion([Q0])});
            skLineSegment(sketch, "E37", {"start": v(-55.22, -42.78) * mm, "end": v(-51.56, -58.48) * mm});
            skLineSegment(sketch, "E38", {"start": v(-48.64, -60.93) * mm, "end": v(-32.54, -61.8) * mm});
            skLineSegment(sketch, "E39", {"start": v(32.54, -61.8) * mm, "end": v(48.64, -60.93) * mm});
            skLineSegment(sketch, "E40", {"start": v(51.56, -58.48) * mm, "end": v(55.22, -42.78) * mm});
            skLineSegment(sketch, "E41", {"start": v(-44.9, -53.5) * mm, "end": v(-51.02, -60.8) * mm, "construction": true});
            skLineSegment(sketch, "E42", {"start": v(44.9, -53.5) * mm, "end": v(51.02, -60.8) * mm, "construction": true});
            skCircle(sketch, "E43", {"center": v(-46.12, -54.97) * mm, "radius": 1.98 * mm});
            skCircle(sketch, "E44", {"center": v(46.12, -54.97) * mm, "radius": 1.98 * mm});
            skPoint(sketch, "E45.visualSharp", {"position": v(-51.02, -60.8) * mm});
            skArc(sketch, "E45.filletArc", {"start": v(-51.56, -58.48) * mm, "mid": v(-50.51, -60.2) * mm, "end": v(-48.64, -60.93) * mm});
            skPoint(sketch, "E46.visualSharp", {"position": v(51.02, -60.8) * mm});
            skArc(sketch, "E46.filletArc", {"start": v(48.64, -60.93) * mm, "mid": v(50.51, -60.2) * mm, "end": v(51.56, -58.48) * mm});
            skSolve(sketch);
        }
        {
            var Q0;
            Q0=makeQuery(id+"F6.imprint","IMPRINT",FACE,{"disambiguationData":[TD([[makeQuery(id+"F6.imprint","IMPRINT",EDGE,{"derivedFrom":sQuery(id+"F6.wireOp",EDGE,"E37")}),1.0]])]});
            var Q1;
            Q1=makeQuery(id+"F6.imprint","IMPRINT",FACE,{"disambiguationData":[TD([[makeQuery(id+"F6.imprint","IMPRINT",EDGE,{"derivedFrom":sQuery(id+"F6.wireOp",EDGE,"E39")}),1.0]])]});
            var Q2;
            Q2=makeQuery(id+"F1.opExtrude","CAP_FACE",FACE,{"disambiguationData":[OSD([sQuery(id+"F0.wireOp",EDGE,"E0"),sQuery(id+"F0.wireOp",EDGE,"E1"),sQuery(id+"F0.wireOp",EDGE,"E4"),sQuery(id+"F0.wireOp",EDGE,"E6"),sQuery(id+"F0.wireOp",EDGE,"E8"),sQuery(id+"F0.wireOp",EDGE,"E9"),sQuery(id+"F0.wireOp",EDGE,"E10"),sQuery(id+"F0.wireOp",EDGE,"E12.filletArc"),sQuery(id+"F0.wireOp",EDGE,"E13.filletArc"),sQuery(id+"F0.wireOp",EDGE,"E15.1.0"),sQuery(id+"F0.wireOp",EDGE,"E15.1.1"),sQuery(id+"F0.wireOp",EDGE,"E15.1.2"),sQuery(id+"F0.wireOp",EDGE,"E15.1.3"),sQuery(id+"F0.wireOp",EDGE,"E15.1.4"),sQuery(id+"F0.wireOp",EDGE,"E15.1.5"),sQuery(id+"F0.wireOp",EDGE,"E15.1.6"),sQuery(id+"F0.wireOp",EDGE,"E15.2.0"),sQuery(id+"F0.wireOp",EDGE,"E15.2.1"),sQuery(id+"F0.wireOp",EDGE,"E15.2.2"),sQuery(id+"F0.wireOp",EDGE,"E15.2.3"),sQuery(id+"F0.wireOp",EDGE,"E15.2.4"),sQuery(id+"F0.wireOp",EDGE,"E15.2.5"),sQuery(id+"F0.wireOp",EDGE,"E15.2.6"),sQuery(id+"F0.wireOp",EDGE,"E15.3.0"),sQuery(id+"F0.wireOp",EDGE,"E15.3.1"),sQuery(id+"F0.wireOp",EDGE,"E15.3.2"),sQuery(id+"F0.wireOp",EDGE,"E15.3.3"),sQuery(id+"F0.wireOp",EDGE,"E15.3.4"),sQuery(id+"F0.wireOp",EDGE,"E15.3.5"),sQuery(id+"F0.wireOp",EDGE,"E15.3.6"),sQuery(id+"F0.wireOp",EDGE,"E15.4.0"),sQuery(id+"F0.wireOp",EDGE,"E15.4.1"),sQuery(id+"F0.wireOp",EDGE,"E15.4.2"),sQuery(id+"F0.wireOp",EDGE,"E15.4.3"),sQuery(id+"F0.wireOp",EDGE,"E15.4.4"),sQuery(id+"F0.wireOp",EDGE,"E15.4.5"),sQuery(id+"F0.wireOp",EDGE,"E15.4.6"),sQuery(id+"F0.wireOp",EDGE,"E15.5.0"),sQuery(id+"F0.wireOp",EDGE,"E15.5.1"),sQuery(id+"F0.wireOp",EDGE,"E15.5.2"),sQuery(id+"F0.wireOp",EDGE,"E15.5.3"),sQuery(id+"F0.wireOp",EDGE,"E15.5.4"),sQuery(id+"F0.wireOp",EDGE,"E15.5.5"),sQuery(id+"F0.wireOp",EDGE,"E15.5.6"),sQuery(id+"F0.wireOp",EDGE,"E15.6.0"),sQuery(id+"F0.wireOp",EDGE,"E15.6.1"),sQuery(id+"F0.wireOp",EDGE,"E15.6.2"),sQuery(id+"F0.wireOp",EDGE,"E15.6.3"),sQuery(id+"F0.wireOp",EDGE,"E15.6.4"),sQuery(id+"F0.wireOp",EDGE,"E15.6.5"),sQuery(id+"F0.wireOp",EDGE,"E15.6.6"),sQuery(id+"F0.wireOp",EDGE,"E15.7.0"),sQuery(id+"F0.wireOp",EDGE,"E15.7.1"),sQuery(id+"F0.wireOp",EDGE,"E15.7.2"),sQuery(id+"F0.wireOp",EDGE,"E15.7.3"),sQuery(id+"F0.wireOp",EDGE,"E15.7.4"),sQuery(id+"F0.wireOp",EDGE,"E15.7.5"),sQuery(id+"F0.wireOp",EDGE,"E15.7.6"),sQuery(id+"F0.wireOp",EDGE,"E15.8.0"),sQuery(id+"F0.wireOp",EDGE,"E15.8.1"),sQuery(id+"F0.wireOp",EDGE,"E15.8.2"),sQuery(id+"F0.wireOp",EDGE,"E15.8.3"),sQuery(id+"F0.wireOp",EDGE,"E15.8.4"),sQuery(id+"F0.wireOp",EDGE,"E15.8.5"),sQuery(id+"F0.wireOp",EDGE,"E15.8.6"),sQuery(id+"F0.wireOp",EDGE,"E16"),sQuery(id+"F0.wireOp",EDGE,"E17"),sQuery(id+"F0.wireOp",EDGE,"E18"),sQuery(id+"F0.wireOp",EDGE,"E21.MirrorC"),sQuery(id+"F0.wireOp",EDGE,"E22.MirrorC"),sQuery(id+"F0.wireOp",EDGE,"E23.MirrorC"),sQuery(id+"F0.wireOp",EDGE,"E24"),sQuery(id+"F0.wireOp",EDGE,"E25"),sQuery(id+"F0.wireOp",EDGE,"E26"),sQuery(id+"F0.wireOp",EDGE,"E27")])],"isStart":true});
            extrude(context, id + "F7", {"entities" : qUnion([Q0, Q1]), "operationType" : NewBodyOperationType.ADD, "endBound" : BoundingType.UP_TO_SURFACE, "oppositeDirection" : true, "endBoundEntityFace" : qUnion([Q2]), "depth" : 25.4 * mm});
        }
    });
